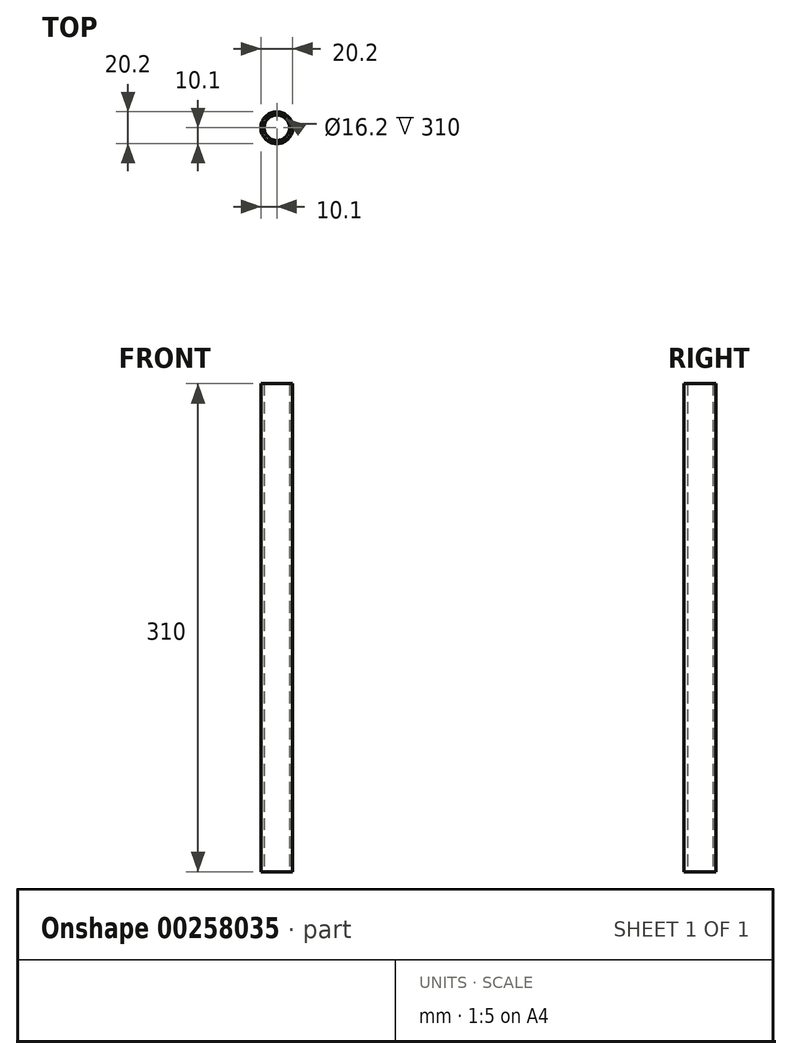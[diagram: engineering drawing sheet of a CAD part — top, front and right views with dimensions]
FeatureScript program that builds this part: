
annotation { "Feature Type Name" : "Feature", "Feature Type Description" : "" }
export const myFeature = defineFeature(function(context is Context, id is Id, definition is map)
    precondition{}
    {
        {
            var Q0;
            Q0=qCreatedBy(makeId("Top.planeOp"),FACE);
            var sketch = newSketch(context, id + "F0", { "sketchPlane" : qUnion([Q0])});
            skCircle(sketch, "E0", {"center": v(0, 0) * mm, "radius": 10.1 * mm});
            skLineSegment(sketch, "E1", {"start": v(0, 15) * mm, "end": v(0, -15) * mm, "construction": true});
            skLineSegment(sketch, "E2", {"start": v(-15, 0) * mm, "end": v(15, 0) * mm, "construction": true});
            skCircle(sketch, "E3.0", {"center": v(0, 0) * mm, "radius": 8.1 * mm});
            skSolve(sketch);
        }
        {
            var Q0;
            Q0 = qSketchRegion(id + "F0", true);
            extrude(context, id + "F1", {"entities" : qUnion([Q0]), "depth" : 310 * mm});
        }
    });
